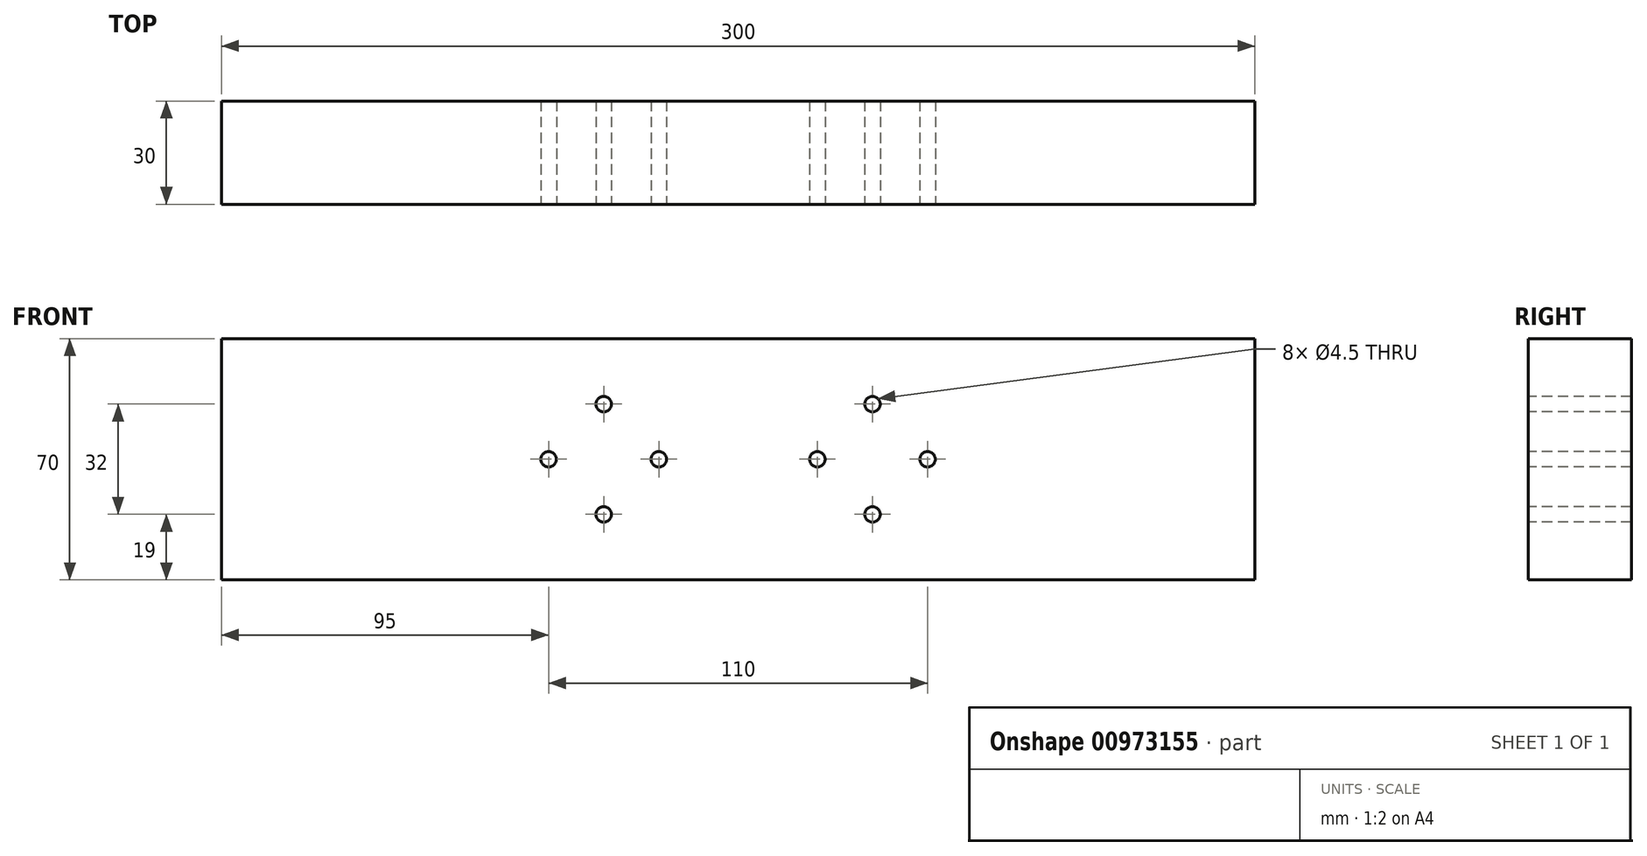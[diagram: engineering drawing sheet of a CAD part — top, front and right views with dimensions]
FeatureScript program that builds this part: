
annotation { "Feature Type Name" : "Feature", "Feature Type Description" : "" }
export const myFeature = defineFeature(function(context is Context, id is Id, definition is map)
    precondition{}
    {
        {
            var Q0;
            Q0=qCreatedBy(makeId("Front.planeOp"),FACE);
            var sketch = newSketch(context, id + "F0", { "sketchPlane" : qUnion([Q0])});
            skLineSegment(sketch, "E0.bottom", {"start": v(150, 35) * mm, "end": v(-150, 35) * mm});
            skLineSegment(sketch, "E0.top", {"start": v(150, -35) * mm, "end": v(-150, -35) * mm});
            skLineSegment(sketch, "E0.left", {"start": v(150, 35) * mm, "end": v(150, -35) * mm});
            skLineSegment(sketch, "E0.right", {"start": v(-150, 35) * mm, "end": v(-150, -35) * mm});
            skPoint(sketch, "E0.middle", {"position": v(0, 0) * mm});
            skSolve(sketch);
        }
        {
            var Q0;
            Q0=makeQuery(id+"F0.imprint","IMPRINT",FACE,{"disambiguationData":[TD([[makeQuery(id+"F0.imprint","IMPRINT",EDGE,{"derivedFrom":sQuery(id+"F0.wireOp",EDGE,"E0.bottom")}),1.0]])]});
            extrude(context, id + "F1", {"entities" : qUnion([Q0]), "depth" : 30 * mm, "offsetDistance" : 25 * mm});
        }
        {
            var Q0;
            Q0=makeQuery(id+"F1.opExtrude","CAP_FACE",FACE,{"disambiguationData":[OSD([sQuery(id+"F0.wireOp",EDGE,"E0.bottom"),sQuery(id+"F0.wireOp",EDGE,"E0.top"),sQuery(id+"F0.wireOp",EDGE,"E0.left"),sQuery(id+"F0.wireOp",EDGE,"E0.right")])],"isStart":false});
            var sketch = newSketch(context, id + "F2", { "sketchPlane" : qUnion([Q0])});
            skLineSegment(sketch, "E1", {"start": v(0, -35) * mm, "end": v(0, 35) * mm, "construction": true});
            skLineSegment(sketch, "E2", {"start": v(39, -35) * mm, "end": v(39, 35) * mm, "construction": true});
            skLineSegment(sketch, "E3", {"start": v(-39, -35) * mm, "end": v(-39, 35) * mm, "construction": true});
            skLineSegment(sketch, "E4", {"start": v(23, -35) * mm, "end": v(23, 35) * mm, "construction": true});
            skLineSegment(sketch, "E5", {"start": v(-23, -35) * mm, "end": v(-23, 35) * mm, "construction": true});
            skLineSegment(sketch, "E6", {"start": v(55, -35) * mm, "end": v(55, 35) * mm, "construction": true});
            skLineSegment(sketch, "E7", {"start": v(-55, -35) * mm, "end": v(-55, 35) * mm, "construction": true});
            skLineSegment(sketch, "E8", {"start": v(150, 0) * mm, "end": v(-150, 0) * mm, "construction": true});
            skLineSegment(sketch, "E9", {"start": v(150, -16) * mm, "end": v(-150, -16) * mm, "construction": true});
            skLineSegment(sketch, "E10", {"start": v(150, 16) * mm, "end": v(-150, 16) * mm, "construction": true});
            skCircle(sketch, "E11", {"center": v(39, -16) * mm, "radius": 2.25 * mm});
            skCircle(sketch, "E12", {"center": v(55, 0) * mm, "radius": 2.25 * mm});
            skCircle(sketch, "E13", {"center": v(39, 16) * mm, "radius": 2.25 * mm});
            skCircle(sketch, "E14", {"center": v(23, 0) * mm, "radius": 2.25 * mm});
            skCircle(sketch, "E15", {"center": v(-39, -16) * mm, "radius": 2.25 * mm});
            skCircle(sketch, "E16", {"center": v(-55, 0) * mm, "radius": 2.25 * mm});
            skCircle(sketch, "E17", {"center": v(-23, 0) * mm, "radius": 2.25 * mm});
            skCircle(sketch, "E18", {"center": v(-39, 16) * mm, "radius": 2.25 * mm});
            skSolve(sketch);
        }
        {
            var Q0;
            Q0=makeQuery(id+"F2.imprint","IMPRINT",FACE,{"disambiguationData":[TD([[makeQuery(id+"F2.imprint","IMPRINT",EDGE,{"derivedFrom":sQuery(id+"F2.wireOp",EDGE,"E11")}),1.0]])]});
            var Q1;
            Q1=makeQuery(id+"F2.imprint","IMPRINT",FACE,{"disambiguationData":[TD([[makeQuery(id+"F2.imprint","IMPRINT",EDGE,{"derivedFrom":sQuery(id+"F2.wireOp",EDGE,"E12")}),1.0]])]});
            var Q2;
            Q2=makeQuery(id+"F2.imprint","IMPRINT",FACE,{"disambiguationData":[TD([[makeQuery(id+"F2.imprint","IMPRINT",EDGE,{"derivedFrom":sQuery(id+"F2.wireOp",EDGE,"E13")}),1.0]])]});
            var Q3;
            Q3=makeQuery(id+"F2.imprint","IMPRINT",FACE,{"disambiguationData":[TD([[makeQuery(id+"F2.imprint","IMPRINT",EDGE,{"derivedFrom":sQuery(id+"F2.wireOp",EDGE,"E14")}),1.0]])]});
            var Q4;
            Q4=makeQuery(id+"F2.imprint","IMPRINT",FACE,{"disambiguationData":[TD([[makeQuery(id+"F2.imprint","IMPRINT",EDGE,{"derivedFrom":sQuery(id+"F2.wireOp",EDGE,"E15")}),1.0]])]});
            var Q5;
            Q5=makeQuery(id+"F2.imprint","IMPRINT",FACE,{"disambiguationData":[TD([[makeQuery(id+"F2.imprint","IMPRINT",EDGE,{"derivedFrom":sQuery(id+"F2.wireOp",EDGE,"E18")}),1.0]])]});
            var Q6;
            Q6=makeQuery(id+"F2.imprint","IMPRINT",FACE,{"disambiguationData":[TD([[makeQuery(id+"F2.imprint","IMPRINT",EDGE,{"derivedFrom":sQuery(id+"F2.wireOp",EDGE,"E16")}),1.0]])]});
            var Q7;
            Q7=makeQuery(id+"F2.imprint","IMPRINT",FACE,{"disambiguationData":[TD([[makeQuery(id+"F2.imprint","IMPRINT",EDGE,{"derivedFrom":sQuery(id+"F2.wireOp",EDGE,"E17")}),1.0]])]});
            extrude(context, id + "F3", {"entities" : qUnion([Q0, Q1, Q2, Q3, Q4, Q5, Q6, Q7]), "operationType" : NewBodyOperationType.REMOVE, "endBound" : BoundingType.THROUGH_ALL, "oppositeDirection" : true, "depth" : 25 * mm, "offsetDistance" : 25 * mm});
        }
    });
